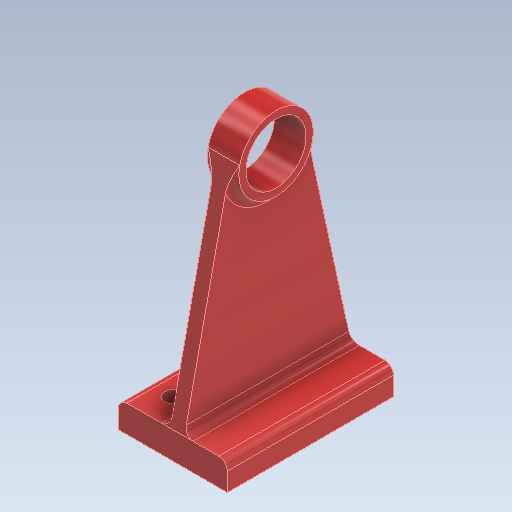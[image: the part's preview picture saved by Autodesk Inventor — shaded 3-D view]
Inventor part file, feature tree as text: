
AUTODESK INVENTOR PART (.ipt)
format: ipt  version: 2021 (Build 250183000, 183)  size: 187,392 bytes
history: native  units: in
note: dims shown in document units (in); Inventor stores cm internally (conversion verified against a paired STEP export)
features: extrude x4, sketch x2, fillet x2
ambient origin geometry x8: Origin, YZ Plane, XZ Plane, XY Plane, X Axis, Y Axis, Z Axis, Center Point
bodies: Solid1 (feature_tree)
feature tree (8):
  sketch  "Sketch1"  dims[d2=0.374in d3=2.2835in]
  extrude  "Extrusion1"  Depth=0.374in
  extrude  "Extrusion2"  Depth=0.3937in
  extrude  "Extrusion3"  Depth=0.3937in
  fillet  "Fillet1"  Radius=1.0236in
  fillet  "Fillet2"  Radius=0.1969in
  extrude  "Extrusion4"  Depth=0.3937in TaperAngle=0.0deg
  sketch  "Sketch2"  dims[d4=1.1417in d5=3.2283in d6=0.8268in d7=1.0236in d8=0.1969in d9=0.0in d10=0.315in d11=0.0in d12=0.1181in d13=0.0in d14=0.7874in d15=0.7087in d16=0.0in d17=0.0in d18=0.1181in d19=0.1181in d20=0.3937in d21=0.3543in d22=0.3937in d23=0.3543in d24=0.2362in d25=0.2362in d26=0.7874in d27=0.0in]
